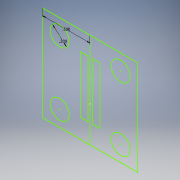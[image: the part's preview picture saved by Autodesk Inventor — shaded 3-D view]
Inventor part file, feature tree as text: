
AUTODESK INVENTOR PART (.ipt)
format: ipt  version: 2018 (Build 220112000, 112)  size: 95,232 bytes
history: native  units: in
note: dims shown in document units (in); Inventor stores cm internally (conversion verified against a paired STEP export)
features: sketch x2
ambient origin geometry x8: Origin, YZ Plane, XZ Plane, XY Plane, X Axis, Y Axis, Z Axis, Center Point
feature tree (2):
  sketch  "Sketch1"  dims[d0=0.5in]
  sketch  "Sketch2"  dims[d2=0.2in]
